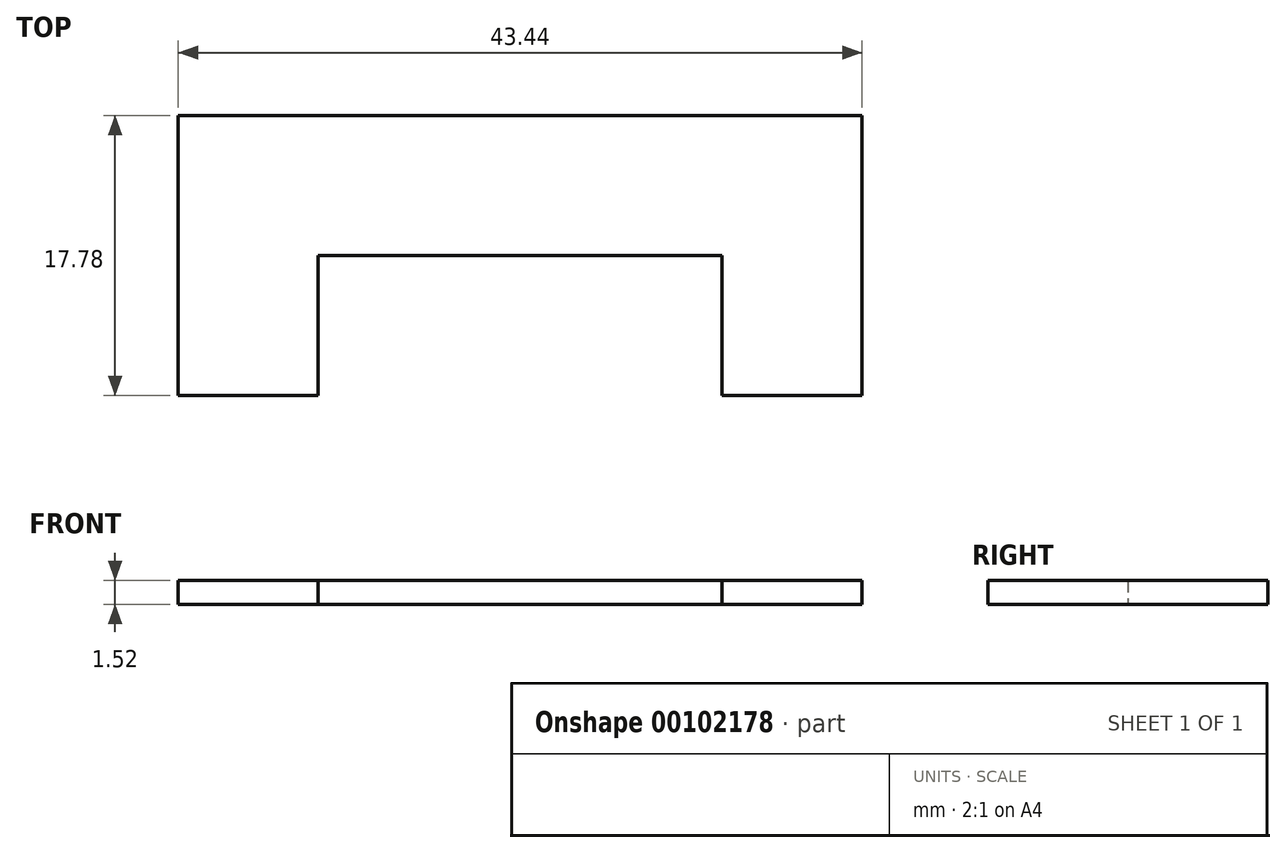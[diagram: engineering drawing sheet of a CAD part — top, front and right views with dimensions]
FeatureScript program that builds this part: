
annotation { "Feature Type Name" : "Feature", "Feature Type Description" : "" }
export const myFeature = defineFeature(function(context is Context, id is Id, definition is map)
    precondition{}
    {
        {
            var Q0;
            Q0=qCreatedBy(makeId("Top.planeOp"),FACE);
            var sketch = newSketch(context, id + "F0", { "sketchPlane" : qUnion([Q0])});
            skLineSegment(sketch, "E0", {"start": v(-21.72, 0) * mm, "end": v(-12.83, 0) * mm});
            skLineSegment(sketch, "E1", {"start": v(-12.83, 0) * mm, "end": v(-12.83, 8.89) * mm});
            skLineSegment(sketch, "E2", {"start": v(-12.83, 8.89) * mm, "end": v(12.83, 8.89) * mm});
            skLineSegment(sketch, "E3", {"start": v(12.83, 8.89) * mm, "end": v(12.83, 0) * mm});
            skLineSegment(sketch, "E4", {"start": v(12.83, 0) * mm, "end": v(21.72, 0) * mm});
            skLineSegment(sketch, "E5", {"start": v(21.72, 0) * mm, "end": v(21.72, 17.78) * mm});
            skLineSegment(sketch, "E6", {"start": v(21.72, 17.78) * mm, "end": v(-21.72, 17.78) * mm});
            skLineSegment(sketch, "E7", {"start": v(-21.72, 17.78) * mm, "end": v(-21.72, 0) * mm});
            skPoint(sketch, "E8", {"position": v(0, 8.89) * mm});
            skLineSegment(sketch, "E9", {"start": v(0, 8.89) * mm, "end": v(0, 17.78) * mm, "construction": true});
            skSolve(sketch);
        }
        {
            var Q0;
            Q0 = qSketchRegion(id + "F0", true);
            extrude(context, id + "F1", {"entities" : qUnion([Q0]), "depth" : 1.52 * mm});
        }
    });
